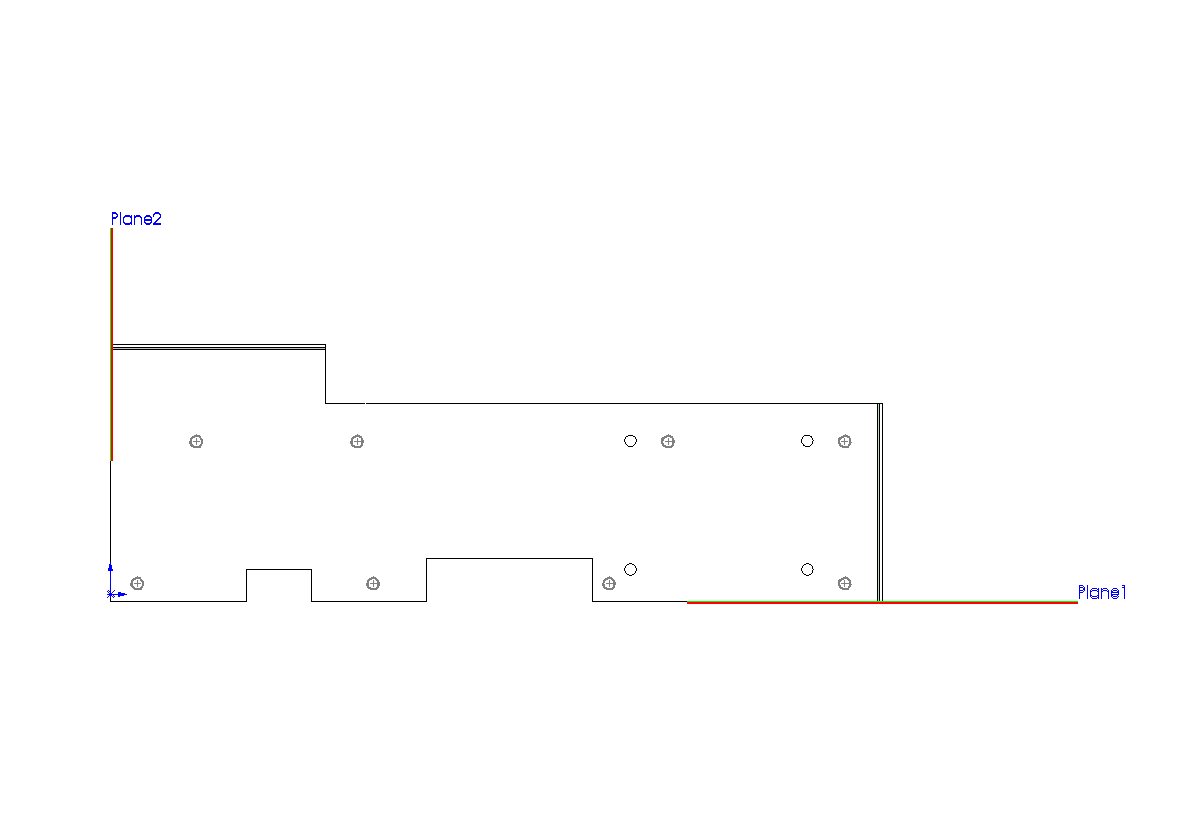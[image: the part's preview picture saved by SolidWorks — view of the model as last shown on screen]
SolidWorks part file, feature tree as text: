
SOLIDWORKS PART (.sldprt)
format: sldprt  version: not decoded by parser v0  size: 247,808 bytes
history: native  units: mm
features: sketch x7, sheet_metal_op x3, cut_extrude x3, plane x2, pattern_linear x2, material x1 + 1 further entry (+14 scaffold rows collapsed)
feature tree (33):
  scaffold x14  (default folders/planes/origin — collapsed)
  material  "Material <not specified>"
  sketch  "Sketch1"  dims[c1.D1=~2.022068mm c2.D1=365.76mm c2.D2=121.92mm c2.D3=76.2mm c2.D4=101.6mm c3.D3=93.98mm c3.D5=152.4mm]
  sheet_metal_op  "Sheet-Metal1"  Thickness=1.524mm
  sheet_metal_op  "Base-Flange1"
  plane  "Plane1"
  sketch  "Sketch4"  dims[c1.D1=17.78mm c2.D1=0.7366mm c2.D4=90.0deg c2.D5=1.0 c2.D8=0.762mm c2.D9=0.762mm c3.D1=0.7366mm c3.D2=500.0mm c3.D3=0.0mm c4.D2=0.0mm c4.D3=0.0mm]
  plane  "Plane2"
  sketch  "Sketch5"  dims[D1=7.62mm Miter Flange2=0.0]
  sheet_metal_op  "Miterbend2"
  sketch  "Sketch6"  dims[c1.D1=5.4102mm c1.D2=5.4102mm c1.D3=5.4102mm c1.D4=5.4102mm c1.D5=5.4102mm c1.D6=5.4102mm c1.D7=5.4102mm c1.D8=5.4102mm c2.D2=18.034mm c2.D3=111.506mm]
  cut_extrude  "PCB mount holes"  Depth=2.54mm
  sketch  "Sketch7"  dims[c1.D1=5.4102mm c1.D2=5.4102mm c1.D5=5.4102mm c2.D1=7.62mm c2.D2=25.4mm c2.D3=20.32mm c2.D4=30.48mm c2.D5=29.21mm c2.D6=15.24mm c3.D1=119.38mm c3.D2=54.61mm c3.D5=64.516mm]
  cut_extrude  "Cut-Extrude2"  Depth=2.54mm
  sketch  "Sketch8"  dims[D1=5.4102mm D2=330.2mm D3=15.24mm]
  cut_extrude  "Cut-Extrude3"  Depth=2.54mm
  pattern_linear  "LPattern1"  Count1=2 Count2=2 Spacing1=83.82mm Spacing2=60.96mm
  "Flat-Pattern1"
  sketch  "Bend-Lines1"
  pattern_linear  "Flatten-<Miterbend2>1"  [2 undecoded]
decode coverage: 11 of 15 modeling features carry decoded parameters; 1 rows unclassified (native names shown)
note: ~ marks probable driven/reference dimensions
note: 2 parameter values undecoded
note: suppression state not decoded; provenance and decode notes live in map.json
